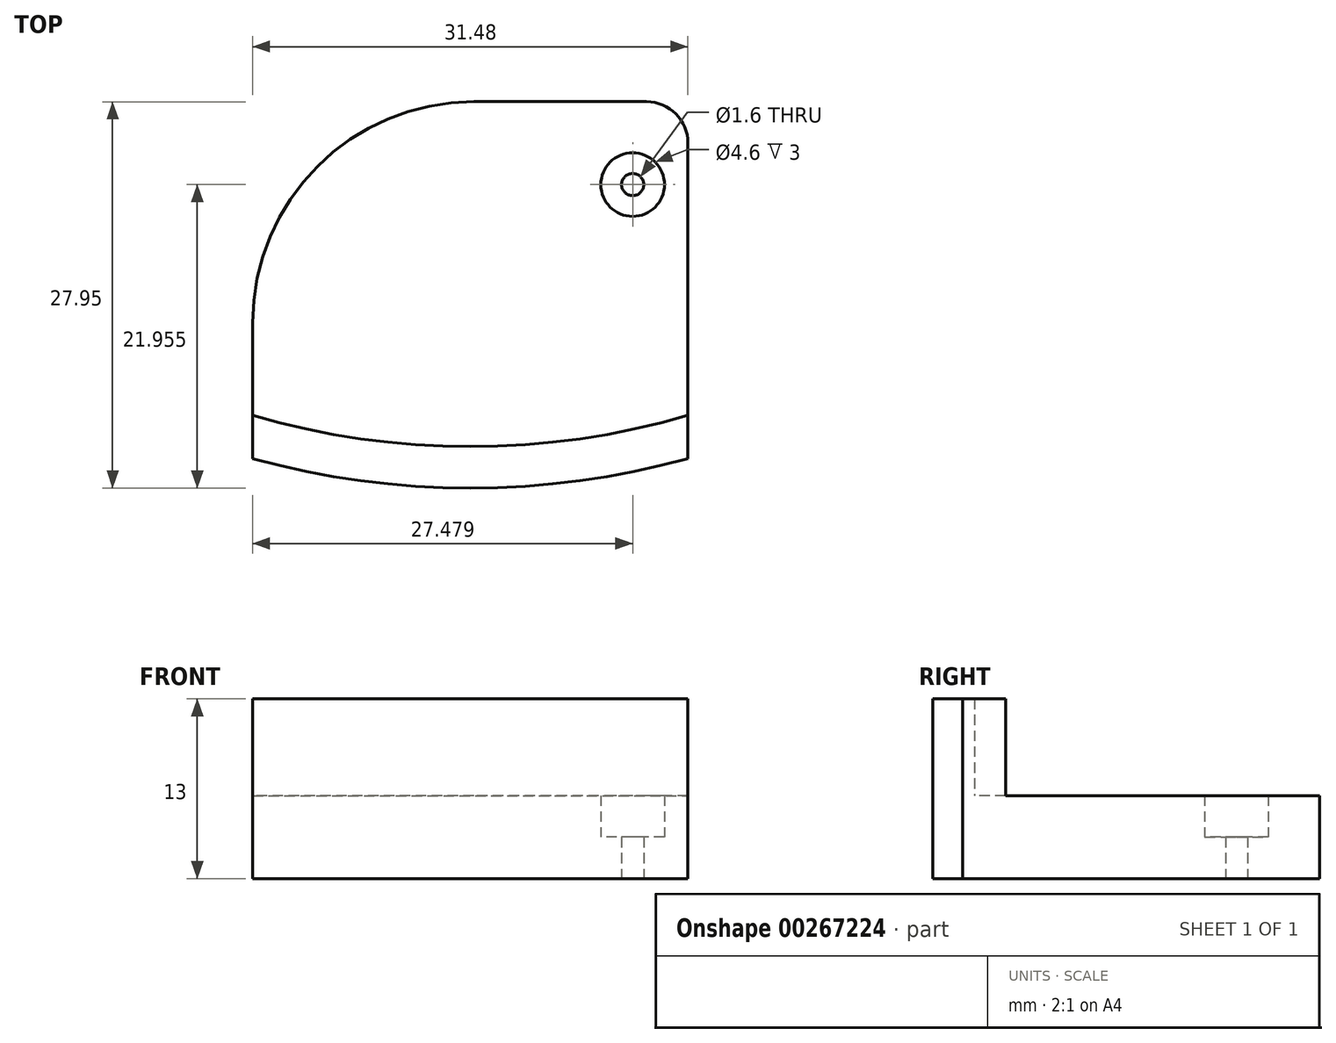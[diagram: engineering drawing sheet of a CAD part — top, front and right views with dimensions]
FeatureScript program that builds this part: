
annotation { "Feature Type Name" : "Feature", "Feature Type Description" : "" }
export const myFeature = defineFeature(function(context is Context, id is Id, definition is map)
    precondition{}
    {
        {
            var Q0;
            Q0=qCreatedBy(makeId("Top.planeOp"),FACE);
            var sketch = newSketch(context, id + "F0", { "sketchPlane" : qUnion([Q0])});
            skCircle(sketch, "E0", {"center": v(11.74, -37.05) * mm, "radius": 0.8 * mm});
            skLineSegment(sketch, "E1.top", {"start": v(15.74, -31.05) * mm, "end": v(-15.74, -31.05) * mm});
            skLineSegment(sketch, "E1.left", {"start": v(15.74, -56.86) * mm, "end": v(15.74, -31.05) * mm});
            skLineSegment(sketch, "E1.right", {"start": v(-15.74, -56.86) * mm, "end": v(-15.74, -31.05) * mm});
            skPoint(sketch, "E1.middle", {"position": v(0, -47.5) * mm});
            skArc(sketch, "E2.0", {"start": v(-15.74, -56.86) * mm, "mid": v(0, -59) * mm, "end": v(15.74, -56.86) * mm});
            skPoint(sketch, "E3.orphan", {"position": v(-15.74, -63.95) * mm});
            skPoint(sketch, "E4.orphan", {"position": v(15.74, -63.95) * mm});
            skSolve(sketch);
        }
        {
            var Q0;
            Q0 = qSketchRegion(id + "F0", true);
            extrude(context, id + "F1", {"entities" : qUnion([Q0]), "depth" : 3 * mm});
        }
        {
            var Q0;
            Q0=makeQuery(id+"F1.opExtrude","CAP_FACE",FACE,{"disambiguationData":[OSD([sQuery(id+"F0.wireOp",EDGE,"E0"),sQuery(id+"F0.wireOp",EDGE,"E1.top"),sQuery(id+"F0.wireOp",EDGE,"E1.left"),sQuery(id+"F0.wireOp",EDGE,"E1.right"),sQuery(id+"F0.wireOp",EDGE,"E2.0")])],"isStart":false});
            var sketch = newSketch(context, id + "F2", { "sketchPlane" : qUnion([Q0])});
            skCircle(sketch, "E5.0", {"center": v(11.74, -37.05) * mm, "radius": 2.3 * mm});
            skSolve(sketch);
        }
        {
            var Q0;
            Q0=makeQuery(id+"F2.imprint","IMPRINT",FACE,{"disambiguationData":[TD([[makeQuery(id+"F2.imprint","IMPRINT",EDGE,{"derivedFrom":sQuery(id+"F2.wireOp",EDGE,"E5.0")}),-1.0]])]});
            extrude(context, id + "F3", {"entities" : qUnion([Q0]), "operationType" : NewBodyOperationType.ADD, "depth" : 3 * mm});
        }
        {
            var Q0;
            Q0=makeQuery(id+"F3.opExtrude","CAP_FACE",FACE,{"disambiguationData":[OSD([sQuery(id+"F0.wireOp",EDGE,"E1.top"),sQuery(id+"F0.wireOp",EDGE,"E1.left"),sQuery(id+"F0.wireOp",EDGE,"E1.right"),sQuery(id+"F0.wireOp",EDGE,"E2.0"),sQuery(id+"F2.wireOp",EDGE,"E5.0")])],"isStart":false});
            var sketch = newSketch(context, id + "F4", { "sketchPlane" : qUnion([Q0])});
            skArc(sketch, "E6.0", {"start": v(-15.74, -53.74) * mm, "mid": v(0, -56) * mm, "end": v(15.74, -53.74) * mm});
            skSolve(sketch);
        }
        {
            var Q0;
            {var subQ0=sQuery(id+"F4.wireOp",EDGE,"E6.0");Q0=makeQuery(id+"F4.imprint","IMPRINT",FACE,{"disambiguationData":[TD([[makeQuery(id+"F4.imprint","IMPRINT",EDGE,{"derivedFrom":subQ0}),-1.0]])]});}
            extrude(context, id + "F5", {"entities" : qUnion([Q0]), "operationType" : NewBodyOperationType.ADD, "depth" : 7 * mm});
        }
        {
            var Q0;
            {var subQ0=sQuery(id+"F0.wireOp",EDGE,"E1.right");var subQ1=sQuery(id+"F0.wireOp",EDGE,"E1.top");Q0=makeQuery(id+"F3.boolean.opBoolean","MERGE",EDGE,{"derivedFrom":[makeQuery(id+"F1.opExtrude","SWEPT_EDGE",EDGE,{"disambiguationData":[OSD([subQ1,subQ0])]}),makeQuery(id+"F3.opExtrude","SWEPT_EDGE",EDGE,{"disambiguationData":[OSD([subQ1,subQ0])]})]});}
            fillet(context, id + "F6", {"entities" : qUnion([Q0]), "radius" : 16 * mm, "tangentPropagation" : true, "allowEdgeOverflow" : false});
        }
        {
            var Q0;
            {var subQ0=sQuery(id+"F0.wireOp",EDGE,"E1.left");var subQ1=sQuery(id+"F0.wireOp",EDGE,"E1.top");Q0=makeQuery(id+"F3.boolean.opBoolean","MERGE",EDGE,{"derivedFrom":[makeQuery(id+"F1.opExtrude","SWEPT_EDGE",EDGE,{"disambiguationData":[OSD([subQ1,subQ0])]}),makeQuery(id+"F3.opExtrude","SWEPT_EDGE",EDGE,{"disambiguationData":[OSD([subQ1,subQ0])]})]});}
            fillet(context, id + "F7", {"entities" : qUnion([Q0]), "radius" : 3 * mm, "tangentPropagation" : true, "allowEdgeOverflow" : false});
        }
    });
